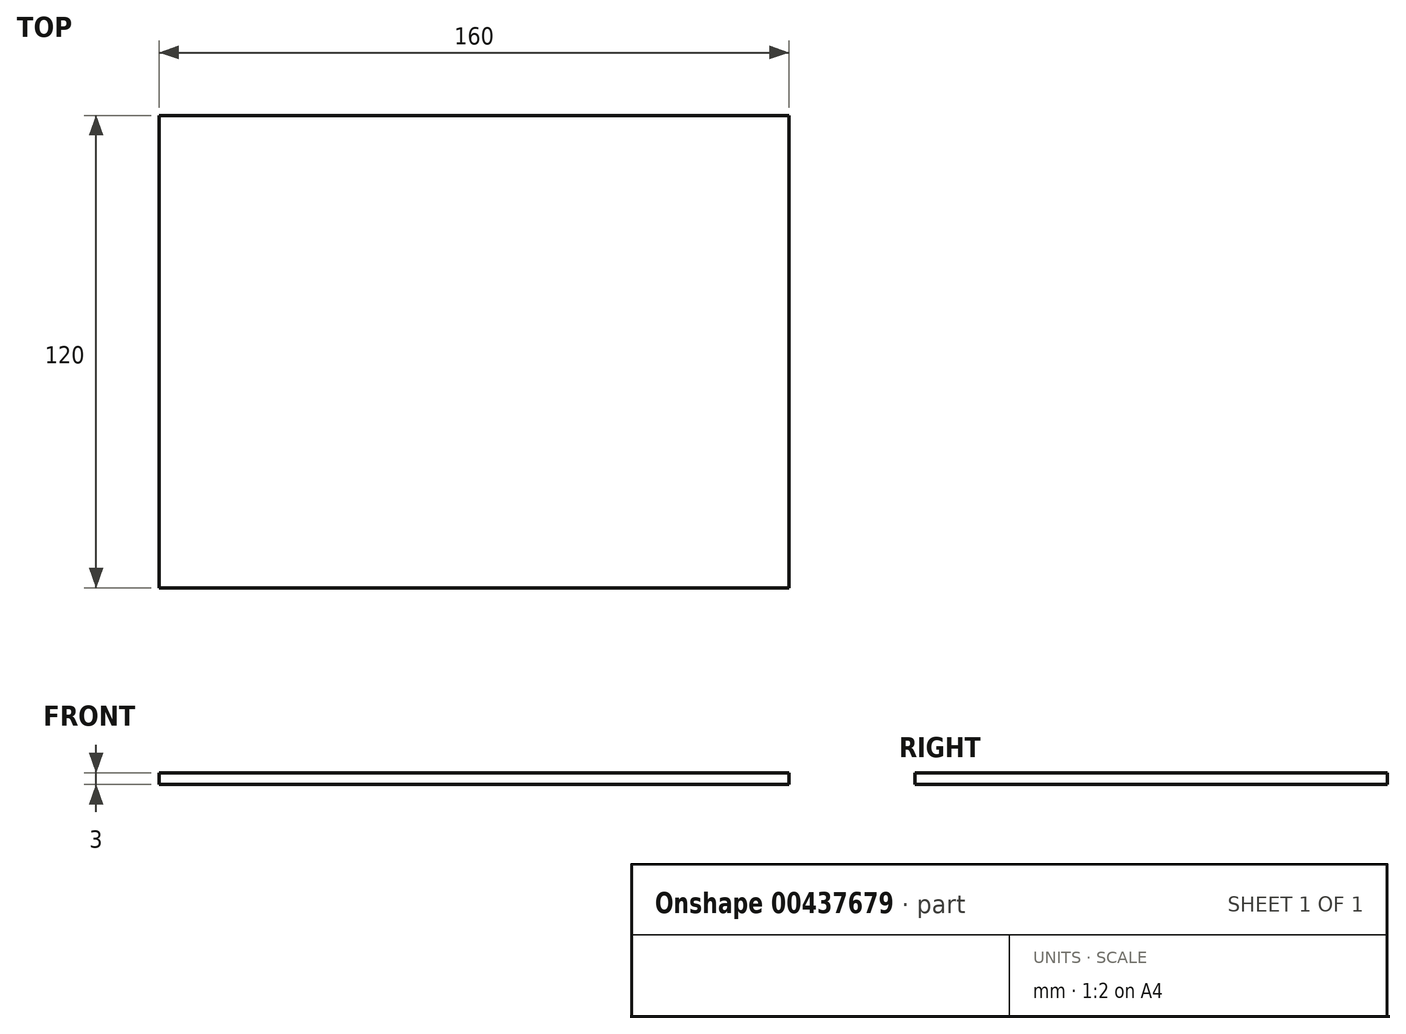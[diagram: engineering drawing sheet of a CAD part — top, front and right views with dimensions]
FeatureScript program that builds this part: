
annotation { "Feature Type Name" : "Feature", "Feature Type Description" : "" }
export const myFeature = defineFeature(function(context is Context, id is Id, definition is map)
    precondition{}
    {
        {
            var Q0;
            Q0=qCreatedBy(makeId("Top.planeOp"),FACE);
            var sketch = newSketch(context, id + "F0", { "sketchPlane" : qUnion([Q0])});
            skLineSegment(sketch, "E0.bottom", {"start": v(80, -60) * mm, "end": v(-80, -60) * mm});
            skLineSegment(sketch, "E0.top", {"start": v(80, 60) * mm, "end": v(-80, 60) * mm});
            skLineSegment(sketch, "E0.left", {"start": v(80, -60) * mm, "end": v(80, 60) * mm});
            skLineSegment(sketch, "E0.right", {"start": v(-80, -60) * mm, "end": v(-80, 60) * mm});
            skPoint(sketch, "E0.middle", {"position": v(0, 0) * mm});
            skSolve(sketch);
        }
        {
            var Q0;
            Q0=makeQuery(id+"F0.imprint","IMPRINT",FACE,{"disambiguationData":[TD([[makeQuery(id+"F0.imprint","IMPRINT",EDGE,{"derivedFrom":sQuery(id+"F0.wireOp",EDGE,"E0.bottom")}),-1.0]])]});
            extrude(context, id + "F1", {"entities" : qUnion([Q0]), "depth" : 3 * mm});
        }
    });
